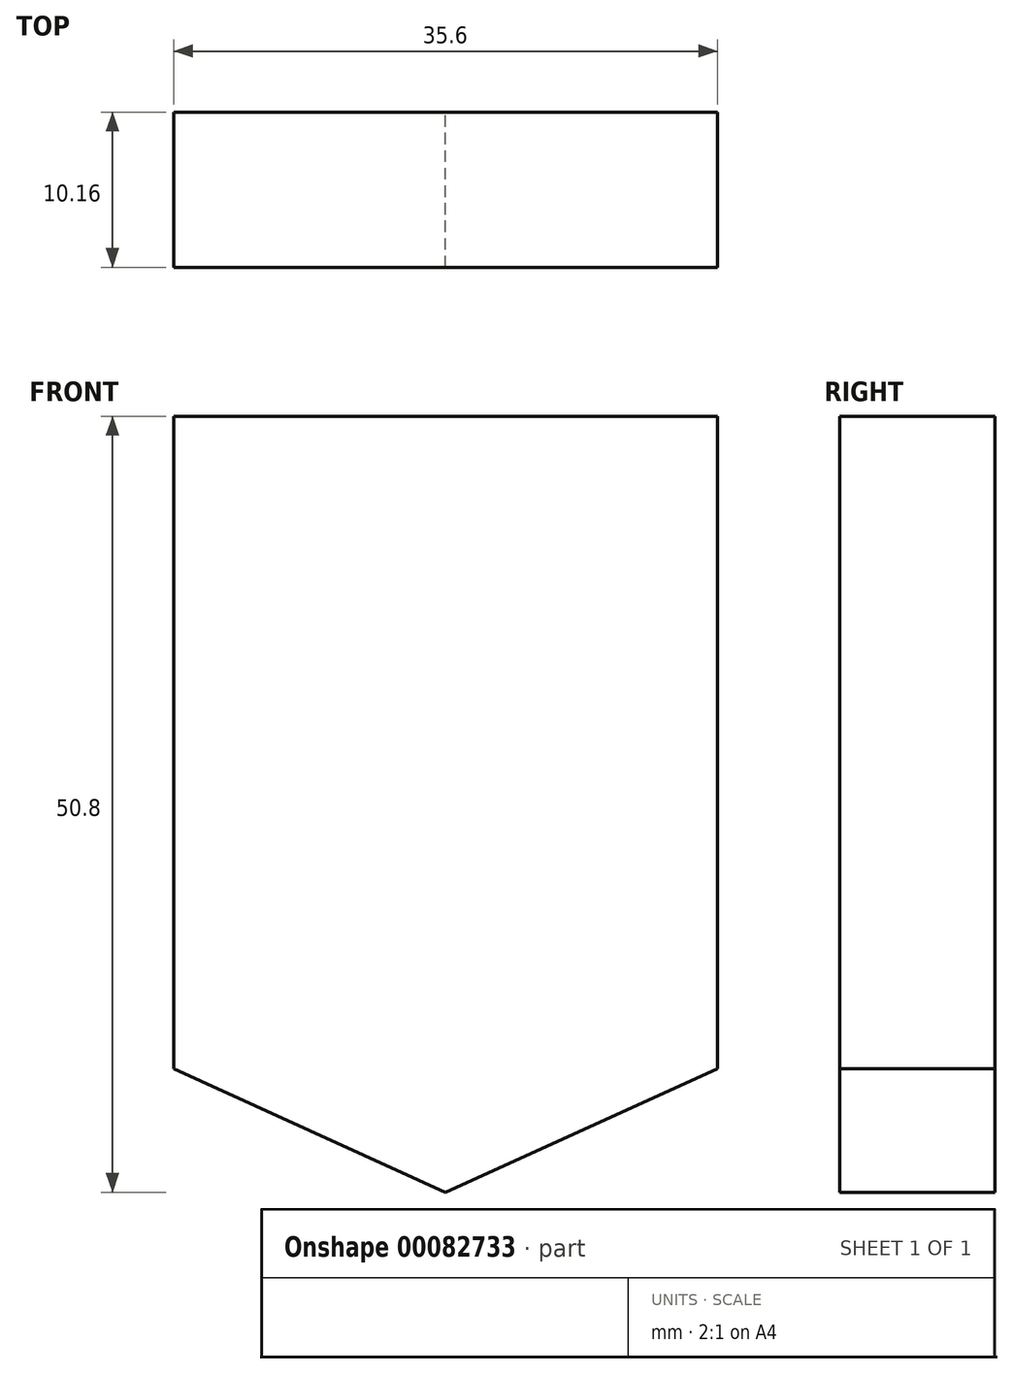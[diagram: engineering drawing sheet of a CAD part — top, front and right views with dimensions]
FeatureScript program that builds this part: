
annotation { "Feature Type Name" : "Feature", "Feature Type Description" : "" }
export const myFeature = defineFeature(function(context is Context, id is Id, definition is map)
    precondition{}
    {
        {
            var Q0;
            Q0=qCreatedBy(makeId("Front.planeOp"),FACE);
            var sketch = newSketch(context, id + "F0", { "sketchPlane" : qUnion([Q0])});
            skLineSegment(sketch, "E0.bottom", {"start": v(25.4, 25.4) * mm, "end": v(-25.4, 25.4) * mm});
            skLineSegment(sketch, "E0.top", {"start": v(25.4, -25.4) * mm, "end": v(-25.4, -25.4) * mm});
            skLineSegment(sketch, "E0.left", {"start": v(25.4, 25.4) * mm, "end": v(25.4, -25.4) * mm});
            skLineSegment(sketch, "E0.right", {"start": v(-25.4, 25.4) * mm, "end": v(-25.4, -25.4) * mm});
            skPoint(sketch, "E0.middle", {"position": v(0, 0) * mm});
            skLineSegment(sketch, "E1", {"start": v(-17.8, 25.4) * mm, "end": v(-17.8, -17.33) * mm});
            skLineSegment(sketch, "E2", {"start": v(-17.8, -17.33) * mm, "end": v(0, -25.4) * mm});
            skLineSegment(sketch, "E3", {"start": v(0, -25.4) * mm, "end": v(0, 25.4) * mm, "construction": true});
            skLineSegment(sketch, "E4.MirrorCS", {"start": v(17.8, 25.4) * mm, "end": v(17.8, -17.33) * mm});
            skLineSegment(sketch, "E5.MirrorCS", {"start": v(17.8, -17.33) * mm, "end": v(0, -25.4) * mm});
            skLineSegment(sketch, "E6", {"start": v(-17.8, 25.4) * mm, "end": v(17.8, 25.4) * mm});
            skSolve(sketch);
        }
        {
            var Q0;
            Q0=makeQuery(id+"F0.imprint","IMPRINT",FACE,{"disambiguationData":[TD([[makeQuery(id+"F0.imprint","IMPRINT",EDGE,{"derivedFrom":sQuery(id+"F0.wireOp",EDGE,"E1")}),1.0]])]});
            extrude(context, id + "F1", {"entities" : qUnion([Q0]), "depth" : 10.16 * mm});
        }
    });
